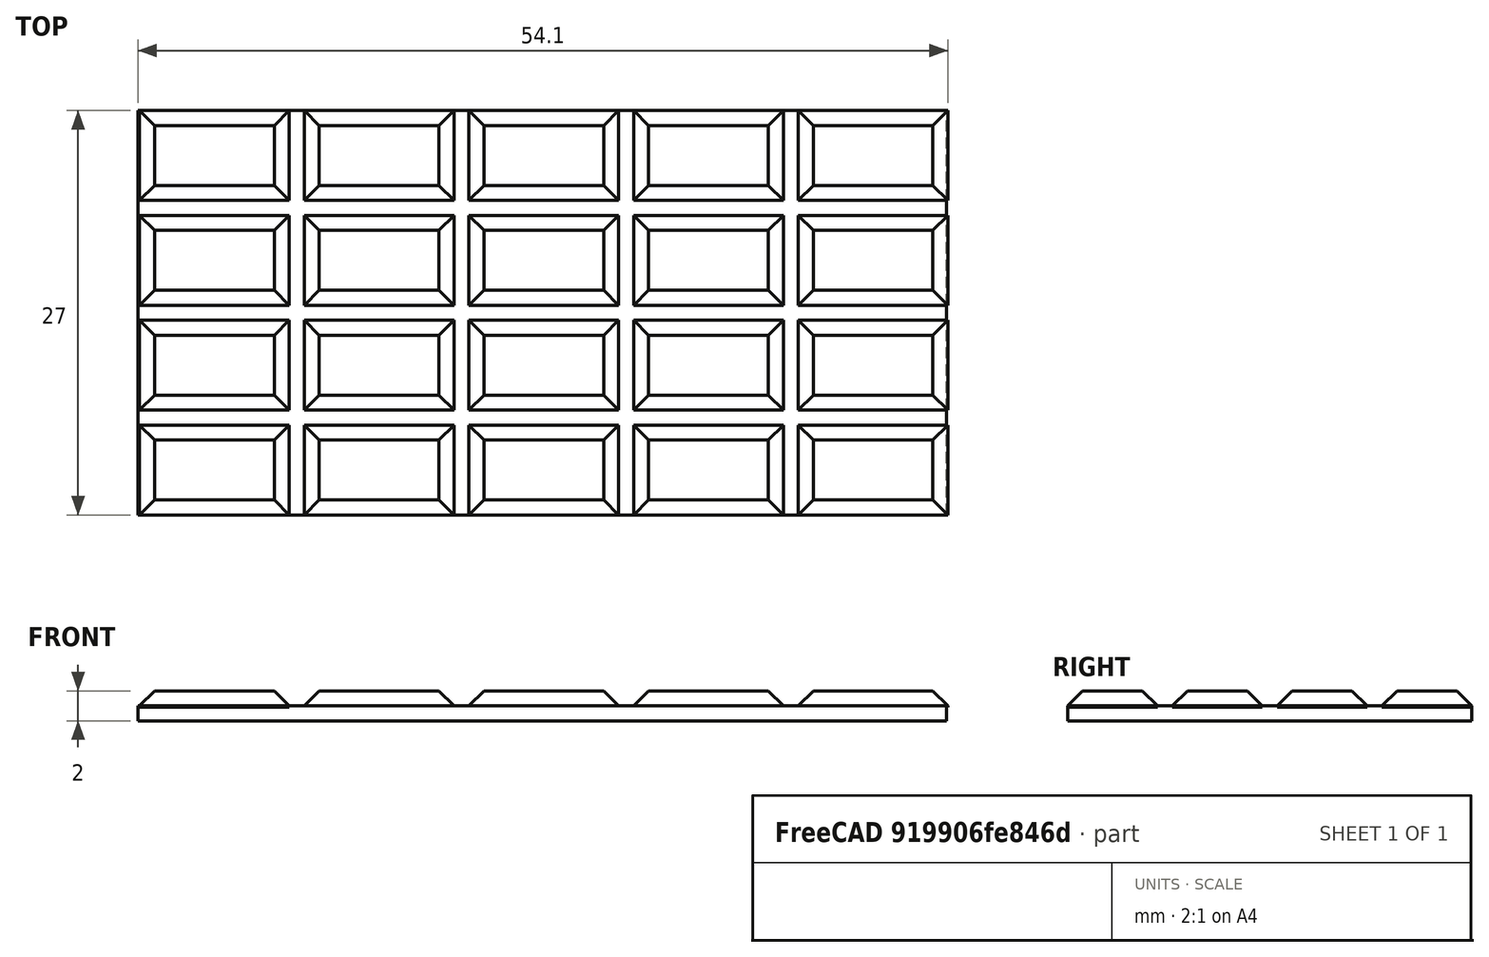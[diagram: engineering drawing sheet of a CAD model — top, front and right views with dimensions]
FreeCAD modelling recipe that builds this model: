
FCSTD DOCUMENT  (FreeCAD 1.0R39319 (Git))
Label: ojt1_t12r02_chocolat
License: All rights reserved
LicenseURL: https://en.wikipedia.org/wiki/All_rights_reserved
objects: Part::Box×2, Part::Chamfer×1, Part::FeaturePython×1, Part::MultiFuse×1
note: 4 computed .brp shape members not serialized (recipe doc carries the construction recipe); baked Part::Feature solids carry a one-line shape summary decoded from their .brp

FEATURE [Part::Box] Box  label="Cub"
  AttacherType = Attacher::AttachEngine3D
  Height = 1
  Length = 54
  Width = 27
FEATURE [Part::Box] Box001  label="Cub001"
  AttacherType = Attacher::AttachEngine3D
  Height = 1.1
  Length = 10
  Placement = pos=(-13,0,0) rot=(0,0,1;0rad)
  Width = 6
FEATURE [Part::Chamfer] Chamfer
  Base = -> Box001
  EdgeLinks = -> Box001 [Edge2,Edge6,Edge10,Edge12]
  Edges = 4 edges r=1: [Edge2,Edge6,Edge10,Edge12]
  Placement = pos=(13.1,0,0.9) rot=(0,0,1;0rad)
FEATURE [Part::FeaturePython] Array  # Draft array (typed FeaturePython)
  AlwaysSyncPlacement = false
  Angle = 360
  ArrayType = 0
  Axis = (0,0,1)
  Base = -> Chamfer
  Center = (0,0,0)
  Count = 20
  ExpandArray = false
  Fuse = false
  IntervalAxis = (0,0,0)
  IntervalX = (11,0,0)
  IntervalY = (0,7,0)
  IntervalZ = (0,0,100)
  NumberCircles = 3
  NumberPolar = 5
  NumberX = 5
  NumberY = 4
  NumberZ = 1
  PlacementList = 20 placements: [(13.1,0,0.9),(13.1,7,0.9),(13.1,14,0.9),(13.1,21,0.9),(24.1,0,0.9),(24.1,7,0.9),(24.1,14,0.9),(24.1,21,0.9),(35.1,0,0.9),(35.1,7,0.9),(35.1,14,0.9),(35.1,21,0.9),(46.1,0,0.9),(46.1,7,0.9),(46.1,14,0.9),(46.1,21,0.9),(57.1,0,0.9),(57.1,7,0.9),(57.1,14,0.9),(57.1,21,0.9)]
  RadialDistance = 50
  ScaleList = (20) [(1,1,1),(1,1,1),(1,1,1),(1,1,1),(1,1,1),(1,1,1),(1,1,1),(1,1,1),(1,1,1),(1,1,1),(1,1,1),(1,1,1),(1,1,1),(1,1,1),(1,1,1),(1,1,1),(1,1,1),(1,1,1),(1,1,1),(1,1,1)]
  Symmetry = 1
  TangentialDistance = 25
FEATURE [Part::MultiFuse] Fusion
  Refine = true
  Shapes = -> [Array,Box]
